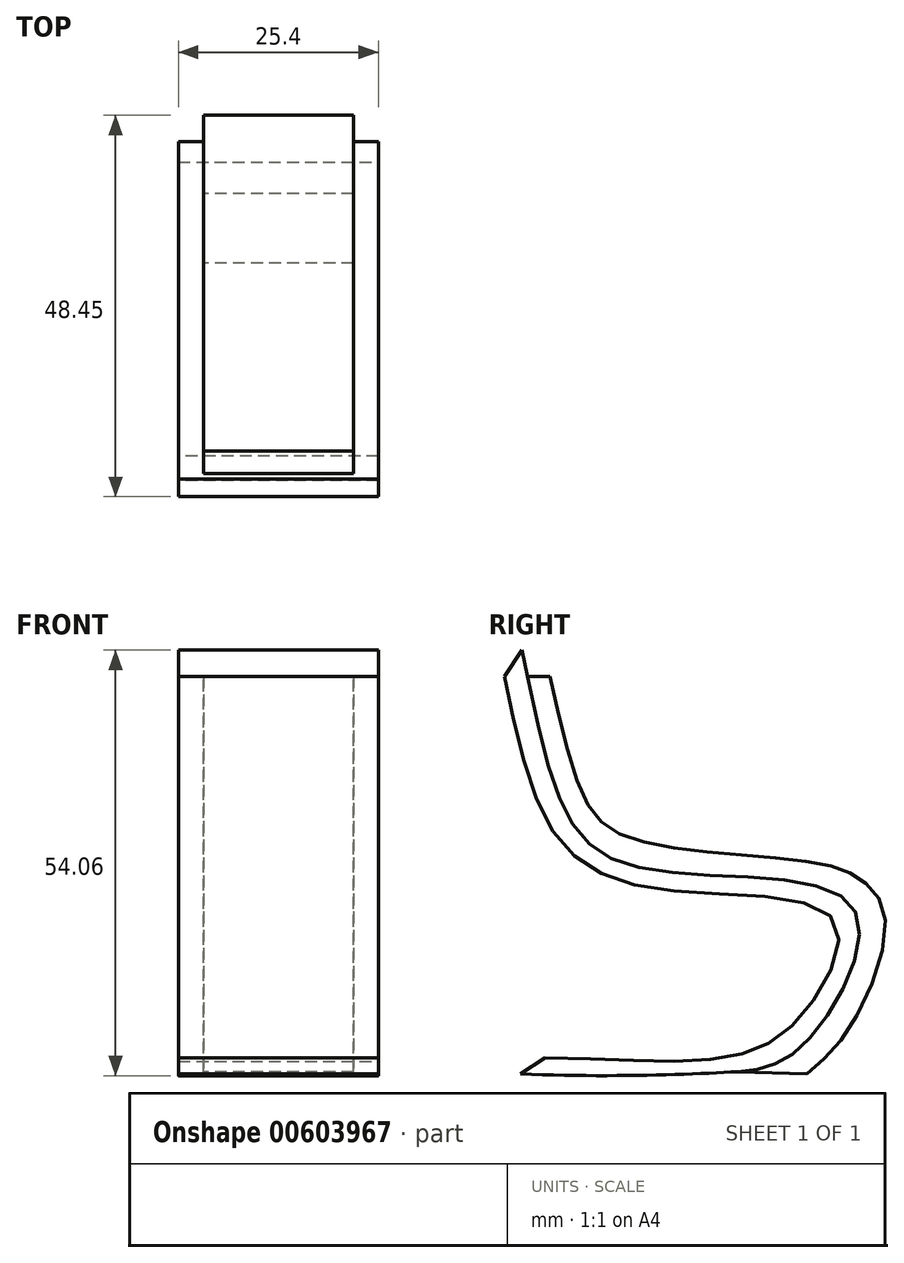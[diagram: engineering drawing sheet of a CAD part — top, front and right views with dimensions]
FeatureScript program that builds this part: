
annotation { "Feature Type Name" : "Feature", "Feature Type Description" : "" }
export const myFeature = defineFeature(function(context is Context, id is Id, definition is map)
    precondition{}
    {
        {
            var Q0;
            Q0=qCreatedBy(makeId("Right.planeOp"),FACE);
            var sketch = newSketch(context, id + "F0", { "sketchPlane" : qUnion([Q0])});
            skFitSpline(sketch, "E0", {"points": [v(-19.63, -24.61) * mm, v(6.36, -24.43) * mm, v(16.37, -20.86) * mm, v(22.57, -3.37) * mm, v(-5.55, 1.85) * mm, v(-19.45, 29.22) * mm], "startDerivative": vector(137.43, -6.14) * mm, "endDerivative": vector(-47.02, 221.01) * mm});
            skLineSegment(sketch, "E1", {"start": v(-19.63, -24.61) * mm, "end": v(-16.5, -22.58) * mm});
            skLineSegment(sketch, "E2", {"start": v(-19.45, 29.22) * mm, "end": v(-21.66, 25.9) * mm});
            skFitSpline(sketch, "E3", {"points": [v(-16.5, -22.58) * mm, v(6.18, -22.58) * mm, v(16.37, -16.87) * mm, v(20.19, -5.07) * mm, v(0, -1.38) * mm, v(-14.66, 5.07) * mm, v(-21.66, 25.9) * mm], "startDerivative": vector(133.78, -0.15) * mm, "endDerivative": vector(-26.53, 125.84) * mm});
            skLineSegment(sketch, "E4", {"start": v(-18.75, 25.9) * mm, "end": v(-15.88, 25.9) * mm});
            skFitSpline(sketch, "E5", {"points": [v(-15.88, 25.9) * mm, v(-11.5, 10.49) * mm, v(-7.1, 5.9) * mm, v(4.7, 3.52) * mm, v(18.56, 2.08) * mm, v(23.72, 0) * mm, v(26.74, -4.74) * mm, v(22.4, -18.5) * mm, v(16.8, -24.59) * mm], "startDerivative": vector(24.78, -111.3) * mm, "endDerivative": vector(-49.18, -41.71) * mm});
            skLineSegment(sketch, "E6", {"start": v(16.8, -24.59) * mm, "end": v(7.98, -24.33) * mm});
            skSolve(sketch);
        }
        {
            var Q0;
            {var subQ0=sQuery(id+"F0.wireOp",EDGE,"E1");Q0=makeQuery(id+"F0.imprint","IMPRINT",FACE,{"disambiguationData":[TD([[makeQuery(id+"F0.imprint","IMPRINT",EDGE,{"derivedFrom":subQ0}),-1.0]])]});}
            extrude(context, id + "F1", {"entities" : qUnion([Q0]), "endBound" : BoundingType.SYMMETRIC, "depth" : 25.4 * mm, "offsetDistance" : 25.4 * mm});
        }
        {
            var Q0;
            {var subQ0=sQuery(id+"F0.wireOp",EDGE,"E4");Q0=makeQuery(id+"F0.imprint","IMPRINT",FACE,{"disambiguationData":[TD([[makeQuery(id+"F0.imprint","IMPRINT",EDGE,{"derivedFrom":subQ0}),-1.0]])]});}
            extrude(context, id + "F2", {"entities" : qUnion([Q0]), "operationType" : NewBodyOperationType.ADD, "endBound" : BoundingType.SYMMETRIC, "depth" : 19.05 * mm, "offsetDistance" : 25.4 * mm});
        }
    });
